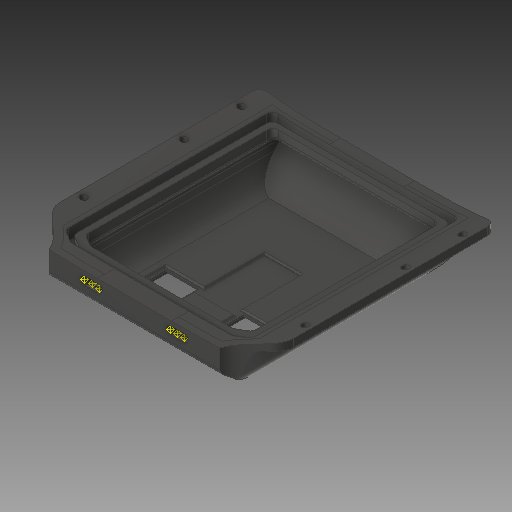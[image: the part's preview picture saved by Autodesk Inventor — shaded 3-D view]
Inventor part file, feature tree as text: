
AUTODESK INVENTOR PART (.ipt)
format: ipt  version: 2019.3 (Build 233278000, 278)  size: 4,955,648 bytes
history: native  units: mm
features: extrude x13, sketch x11, other x10, fillet x7, chamfer x6, plane x3, loft x2, shell x1, emboss x1, projected_geometry x1
ambient origin geometry x8: Origin, YZ Plane, XZ Plane, XY Plane, X Axis, Y Axis, Z Axis, Center Point
bodies: Solid2 (feature_tree), Solid1 (feature_tree)
feature tree (55):
  other  "deck.ipt"
  extrude  "Extrusion1"  Depth=10.0mm
  chamfer  "Chamfer1"  Distance=170.0mm
  chamfer  "Chamfer2"  Distance=20.0mm Angle=45.0deg
  fillet  "Fillet1"  Radius=5.0mm
  fillet  "Fillet2"  Radius=4.0mm
  extrude  "Extrusion4"  Depth=5.0mm
  shell  "Shell1"  Thickness=5.0mm
  extrude  "Extrusion6"  Depth=10.0mm
  emboss  "Emboss1"
  fillet  "Fillet4"  Radius=200.0mm
  sketch  "Sketch8"  dims[d4=18.0mm]
  sketch  "Sketch9"  dims[d5=12.217305mm]
  plane  "Work Plane5"
  extrude  "Extrusion12"  Depth=0.5mm TaperAngle=0.0deg
  extrude  "Extrusion13"  Depth=10.0mm
  extrude  "Extrusion15"  Depth=10.0mm
  extrude  "Extrusion14"  Depth=10.0mm
  fillet  "Fillet8"  Radius=7.0mm
  fillet  "Fillet9"  Radius=15.0mm
  plane  "Work Plane6"
  sketch  "Sketch14"  dims[d6=12.0mm]
  extrude  "Extrusion18"  Depth=10.0mm
  fillet  "Fillet11"  Radius=0.5mm
  extrude  "Extrusion19"  Depth=10.0mm
  plane  "Work Plane7"
  sketch  "Sketch17"  dims[d30=20.0mm d31=30.0mm d32=45.0deg d33=4.0mm]
  sketch  "Sketch18"  dims[d34=186.25mm d35=0.0mm d37=5.0mm d48=5.0mm]
  loft  "Loft1"
  loft  "Loft2"
  other  "MOTOR1_3"
  other  "MOTOR1_2"
  other  "MOTOR1_1"
  other  "MOTOR2_3"
  other  "MOTOR2_2"
  other  "MOTOR2_1"
  sketch  "Sketch19"  dims[d49=20.0mm d51=40.0mm d52=10.0mm d54=10.0mm d56=20.0mm d58=70.0mm d59=10.0mm d61=10.0mm d63=200.0mm]
  extrude  "Extrusion20"  Depth=10.0mm
  extrude  "Extrusion25"  Depth=10.0mm
  chamfer  "Chamfer5"  Distance=6.0mm
  sketch  "Sketch20"  dims[d64=100.0mm d65=0.0mm d66=0.5mm d67=0.0mm]
  extrude  "Extrusion24"  Depth=10.0mm
  extrude  "Extrusion23"  [1 undecoded]
  chamfer  "Chamfer8"  Distance=10.0mm
  fillet  "Fillet14"  Radius=10.0mm
  chamfer  "Chamfer9"  Distance=10.0mm
  chamfer  "Chamfer10"  Distance=5.0mm
  other  "Solid6::deck.ipt"
  other  "TaggingFeature1"
  other  "Front Profile"
  sketch  "Sketch6"  dims[d0=10.0mm d2=82.0mm]
  sketch  "Sketch7"  dims[d3=35.0mm]
  projected_geometry  "Projected Loop2"
  sketch  "Sketch15"  dims[d7=45.0mm d8=170.0mm d9=0.0mm d26=20.0mm d27=30.0mm d28=45.0deg d29=5.0mm]
  sketch  "Sketch21"  dims[d68=5.0mm d69=18.0mm d70=77.400415mm d71=42.0mm d72=7.0mm d73=15.0mm d74=0.5mm d75=0.5mm d76=3.0mm d77=1.0mm d80=10.0mm d81=3.3mm d82=0.5mm d83=6.0mm d84=3.3mm d97=-25.0mm d98=10.0mm d99=10.0mm d100=10.0mm d101=5.0mm d102=13.0mm d103=0.0mm d104=7.0mm d105=7.0mm d106=7.0mm d108=7.0mm d109=4.0mm d110=4.0mm d111=4.0mm d114=10.0mm d115=0.0mm d116=0.0mm d117=0.0mm d118=8.0mm d119=0.0mm d123=0.0mm d124=4.0mm d125=3.0mm d137=-3.5mm d148=0.6mm d149=0.0mm d150=3.0mm d158=3.0mm d161=4.0mm d164=0.6mm d165=0.6mm d166=0.6mm d170=0.6mm d171=0.0mm d172=23.898481mm d173=23.898mm d174=10.0mm d175=5.5mm d177=30.0mm d180=5.5mm d181=5.5mm d182=2.75mm d183=2.75mm d184=2.75mm d185=2.75mm d186=10.0mm d187=10.0mm d194=0.0mm d195=90.0deg d196=0.6mm d197=0.59953mm d198=0.6mm d199=0.6mm d200=0.6mm d201=0.6mm d202=0.6mm d203=-19.0mm d204=0.0mm d205=90.0deg d206=0.0mm d207=90.0deg d208=0.0mm d209=90.0deg d210=9.0mm d211=9.0mm d212=3.0mm d215=5.0mm d216=5.0mm d217=5.0mm d222=1.5mm d223=0.0mm d224=1.0mm d225=2.0mm d226=45.0deg d238=25.0mm d240=12.0mm d241=10.0mm d242=0.0mm d243=2.0mm d244=1.0mm d245=45.0deg d249=25.0mm d250=25.0mm d251=5.0mm d252=2.5mm d253=0.0mm d254=1.0mm d255=1.0mm d256=1.0mm d257=1.0mm d258=3.0mm d259=0.0mm d260=10.0mm d261=6.0mm d262=2.5mm d263=45.0deg d264=6.0mm d265=2.5mm d266=45.0deg]
note: 1 required parameter value undecoded (feature->parameter linkage not recoverable at this tier; creation-order binding heuristic only, values carry confidence <= 0.55)
